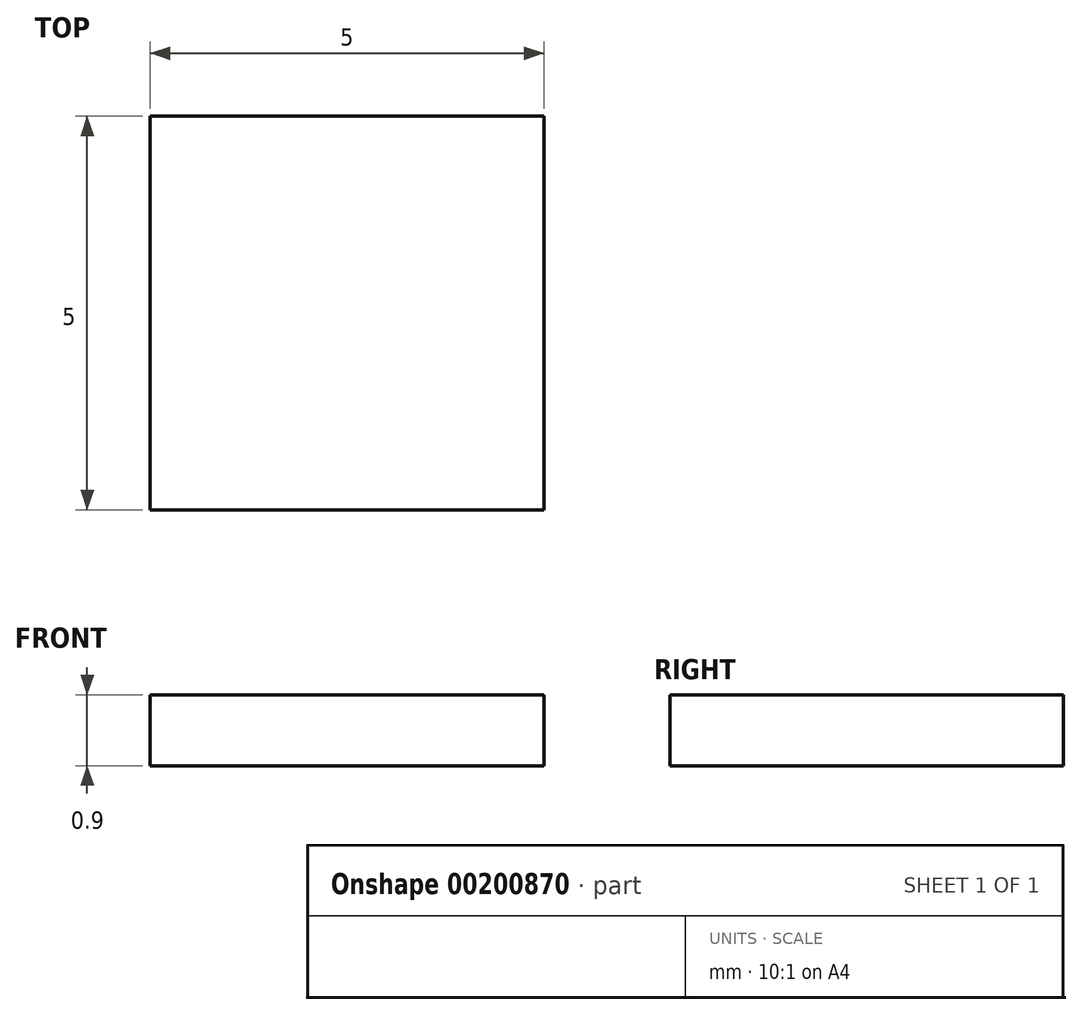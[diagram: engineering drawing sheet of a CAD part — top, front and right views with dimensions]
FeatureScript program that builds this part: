
annotation { "Feature Type Name" : "Feature", "Feature Type Description" : "" }
export const myFeature = defineFeature(function(context is Context, id is Id, definition is map)
    precondition{}
    {
        {
            var Q0;
            Q0=qCreatedBy(makeId("Top.planeOp"),FACE);
            var sketch = newSketch(context, id + "F0", { "sketchPlane" : qUnion([Q0])});
            skLineSegment(sketch, "E0.bottom", {"start": v(2.5, 2.5) * mm, "end": v(-2.5, 2.5) * mm});
            skLineSegment(sketch, "E0.top", {"start": v(2.5, -2.5) * mm, "end": v(-2.5, -2.5) * mm});
            skLineSegment(sketch, "E0.left", {"start": v(2.5, 2.5) * mm, "end": v(2.5, -2.5) * mm});
            skLineSegment(sketch, "E0.right", {"start": v(-2.5, 2.5) * mm, "end": v(-2.5, -2.5) * mm});
            skPoint(sketch, "E0.middle", {"position": v(0, 0) * mm});
            skSolve(sketch);
        }
        {
            var Q0;
            Q0 = qSketchRegion(id + "F0", true);
            extrude(context, id + "F1", {"entities" : qUnion([Q0]), "depth" : .9 * mm});
        }
    });
